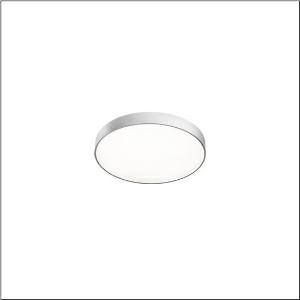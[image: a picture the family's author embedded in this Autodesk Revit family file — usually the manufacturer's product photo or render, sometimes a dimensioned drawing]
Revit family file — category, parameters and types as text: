
# Revit family: round_21_s_51mr34gd0421s
name_source: partatom
category: Lighting Fixtures
units: mm (PartAtom-declared; Revit-internal decimal feet)

## family parameters
Cut with Voids When Loaded = No
Host = Face
Light Source = No
Part Type = Normal
Room Calculation Point = No
Round Connector Dimension = Use Diameter
Shared = No

## types (1)
- Round 21 S (1 x LED, 4090 lm, 28.3 W, 4000K)
    Apparent Load = 28 VA
    CIE Flux Codes = 49 80 96 79 100
    Color Rendering = 80
    Color Temperature = 4000K
    Default Elevation = 1800 mm
    Description = Round 21 S, wall and ceiling luminaire, primary optical cover: cover, of PMMA, opal, light emission: direct/indirect distribution, primary light characteristic: symmetric, installation type: suspended mounting, surface-mounted, LED, rated luminous flux: 4.090lm, luminous efficacy: 135lm/W, light colour: 840, colour temperature: 4000K, control gear: DALI 2, with terminal, 5-pole, mains connection: 230V, AC, 50/60Hz, rated input power: 28.3W, housing, of aluminium, coated, silver, diameter: 400mm, height: 62mm, protection rating (complete): IP40, insulation class (complete): insulation class I (protective earthing), certification: CE, impact resistance: IK04, permissible operating ambient temperature: -10..+35°C, packaging unit: 1 piece
    Height = 87 mm
    Lamp = 1 x LED
    Lamp Light Flux = 4090 lm
    Lamp Power = 28.3 W
    Lamp count = 1
    Length = 400 mm
    Luminous efficacy = 145 lm/W
    Manufacturer = Siteco
    ModVariant = No
    Model = 51MR34GD0421S
    Mounting Place = Ceiling
    Mounting Type = Surface mounted
    Number of Poles = 1
    OnlyDefault = Yes
    Power Factor = 1
    Product Name = Round 21 S
    Product group = wall and ceiling luminaire | ceiling mounted
    ProductGroupID = 304
    Protection Class = Protection class I
    Protection Degree = IP 40
    RLX_Detail_Level = 1
    RLX_Emergency_Light_Flux = 0 lm
    RLX_Emergency_Type = 0
    RLX_Emergency_Type_DB = No
    RlxData = <blob elided: 11577 chars, md5=3528adc4>
    Socket = socket
    Standby Power = 0 W
    System Light Flux = 4090 lm
    System Power = 28 W
    Type Comments = Product without accessories
    Type Image = l_1258309.jpg
    URL = http://relux.com
    VarID = ---
    Voltage = 0 V
    Weight = 0.00 kg
    Width = 0 mm  [stored 0 ft]

note: [stored X ft] marks values corroborated as IEEE doubles in the binary element streams (Revit-internal decimal feet)

## geometry (parser evidence)
native form markers: Sweep x12
no freeform markers — native parametric forms only
